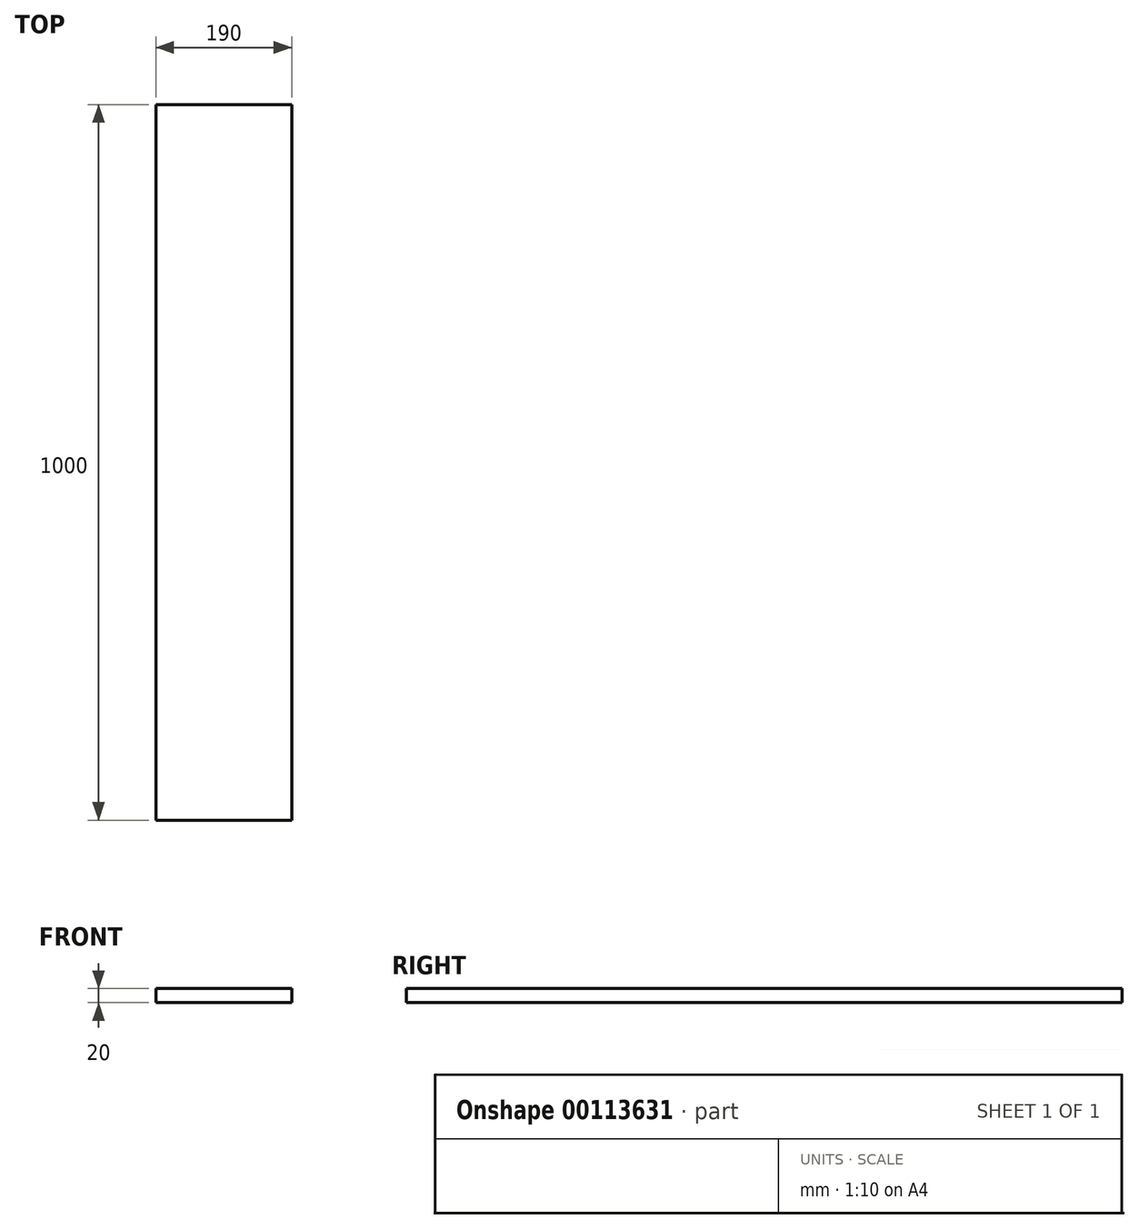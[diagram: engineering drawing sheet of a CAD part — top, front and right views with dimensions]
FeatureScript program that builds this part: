
annotation { "Feature Type Name" : "Feature", "Feature Type Description" : "" }
export const myFeature = defineFeature(function(context is Context, id is Id, definition is map)
    precondition{}
    {
        {
            var Q0;
            Q0=qCreatedBy(makeId("Front.planeOp"),FACE);
            var sketch = newSketch(context, id + "F0", { "sketchPlane" : qUnion([Q0])});
            skLineSegment(sketch, "E0.bottom", {"start": v(0, 0) * mm, "end": v(190, 0) * mm});
            skLineSegment(sketch, "E0.top", {"start": v(0, 20) * mm, "end": v(190, 20) * mm});
            skLineSegment(sketch, "E0.left", {"start": v(0, 0) * mm, "end": v(0, 20) * mm});
            skLineSegment(sketch, "E0.right", {"start": v(190, 0) * mm, "end": v(190, 20) * mm});
            skSolve(sketch);
        }
        {
            var Q0;
            Q0=makeQuery(id+"F0.imprint","IMPRINT",FACE,{"disambiguationData":[TD([[makeQuery(id+"F0.imprint","IMPRINT",EDGE,{"derivedFrom":sQuery(id+"F0.wireOp",EDGE,"E0.bottom")}),1.0]])]});
            extrude(context, id + "F1", {"entities" : qUnion([Q0]), "depth" : 1000 * mm});
        }
    });
